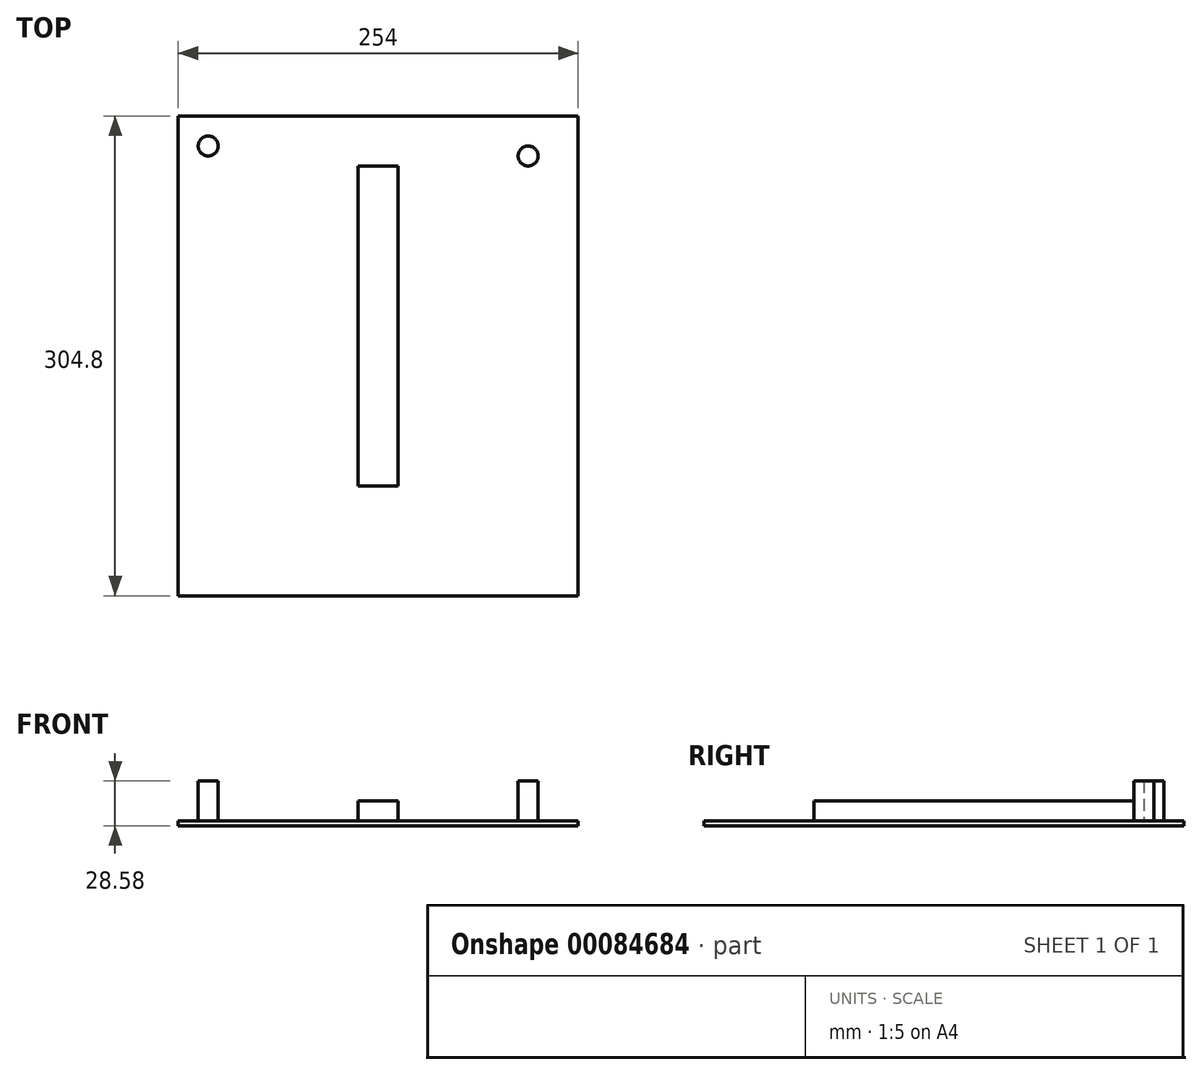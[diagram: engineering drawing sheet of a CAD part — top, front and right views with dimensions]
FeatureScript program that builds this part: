
annotation { "Feature Type Name" : "Feature", "Feature Type Description" : "" }
export const myFeature = defineFeature(function(context is Context, id is Id, definition is map)
    precondition{}
    {
        {
            var Q0;
            Q0=qCreatedBy(makeId("Top.planeOp"),FACE);
            var sketch = newSketch(context, id + "F0", { "sketchPlane" : qUnion([Q0])});
            skLineSegment(sketch, "E0.bottom", {"start": v(0, 0) * mm, "end": v(254, 0) * mm});
            skLineSegment(sketch, "E0.top", {"start": v(0, 304.8) * mm, "end": v(254, 304.8) * mm});
            skLineSegment(sketch, "E0.left", {"start": v(0, 0) * mm, "end": v(0, 304.8) * mm});
            skLineSegment(sketch, "E0.right", {"start": v(254, 0) * mm, "end": v(254, 304.8) * mm});
            skSolve(sketch);
        }
        {
            var Q0;
            Q0=makeQuery(id+"F0.imprint","IMPRINT",FACE,{"disambiguationData":[TD([[makeQuery(id+"F0.imprint","IMPRINT",EDGE,{"derivedFrom":sQuery(id+"F0.wireOp",EDGE,"E0.bottom")}),1.0]])]});
            extrude(context, id + "F1", {"entities" : qUnion([Q0]), "depth" : 3.17 * mm});
        }
        {
            var Q0;
            Q0=makeQuery(id+"F1.opExtrude","CAP_FACE",FACE,{"disambiguationData":[OSD([sQuery(id+"F0.wireOp",EDGE,"E0.bottom"),sQuery(id+"F0.wireOp",EDGE,"E0.top"),sQuery(id+"F0.wireOp",EDGE,"E0.left"),sQuery(id+"F0.wireOp",EDGE,"E0.right")])],"isStart":false});
            var sketch = newSketch(context, id + "F2", { "sketchPlane" : qUnion([Q0])});
            skLineSegment(sketch, "E1.bottom", {"start": v(114.3, 273.03) * mm, "end": v(139.7, 273.03) * mm});
            skLineSegment(sketch, "E1.top", {"start": v(114.3, 69.83) * mm, "end": v(139.7, 69.83) * mm});
            skLineSegment(sketch, "E1.left", {"start": v(114.3, 273.03) * mm, "end": v(114.3, 69.83) * mm});
            skLineSegment(sketch, "E1.right", {"start": v(139.7, 273.03) * mm, "end": v(139.7, 69.83) * mm});
            skSolve(sketch);
        }
        {
            var Q0;
            Q0 = qSketchRegion(id + "F2", true);
            extrude(context, id + "F3", {"entities" : qUnion([Q0]), "operationType" : NewBodyOperationType.ADD, "depth" : 12.7 * mm});
        }
        {
            var Q0;
            Q0=makeQuery(id+"F1.opExtrude","CAP_FACE",FACE,{"disambiguationData":[OSD([sQuery(id+"F0.wireOp",EDGE,"E0.bottom"),sQuery(id+"F0.wireOp",EDGE,"E0.top"),sQuery(id+"F0.wireOp",EDGE,"E0.left"),sQuery(id+"F0.wireOp",EDGE,"E0.right")])],"isStart":false});
            var sketch = newSketch(context, id + "F4", { "sketchPlane" : qUnion([Q0])});
            skCircle(sketch, "E2", {"center": v(222.25, 279.4) * mm, "radius": 6.35 * mm});
            skCircle(sketch, "E3", {"center": v(19.05, 285.75) * mm, "radius": 6.35 * mm});
            skSolve(sketch);
        }
        {
            var Q0;
            Q0 = qSketchRegion(id + "F4", true);
            extrude(context, id + "F5", {"entities" : qUnion([Q0]), "operationType" : NewBodyOperationType.ADD, "depth" : 25.4 * mm});
        }
    });
